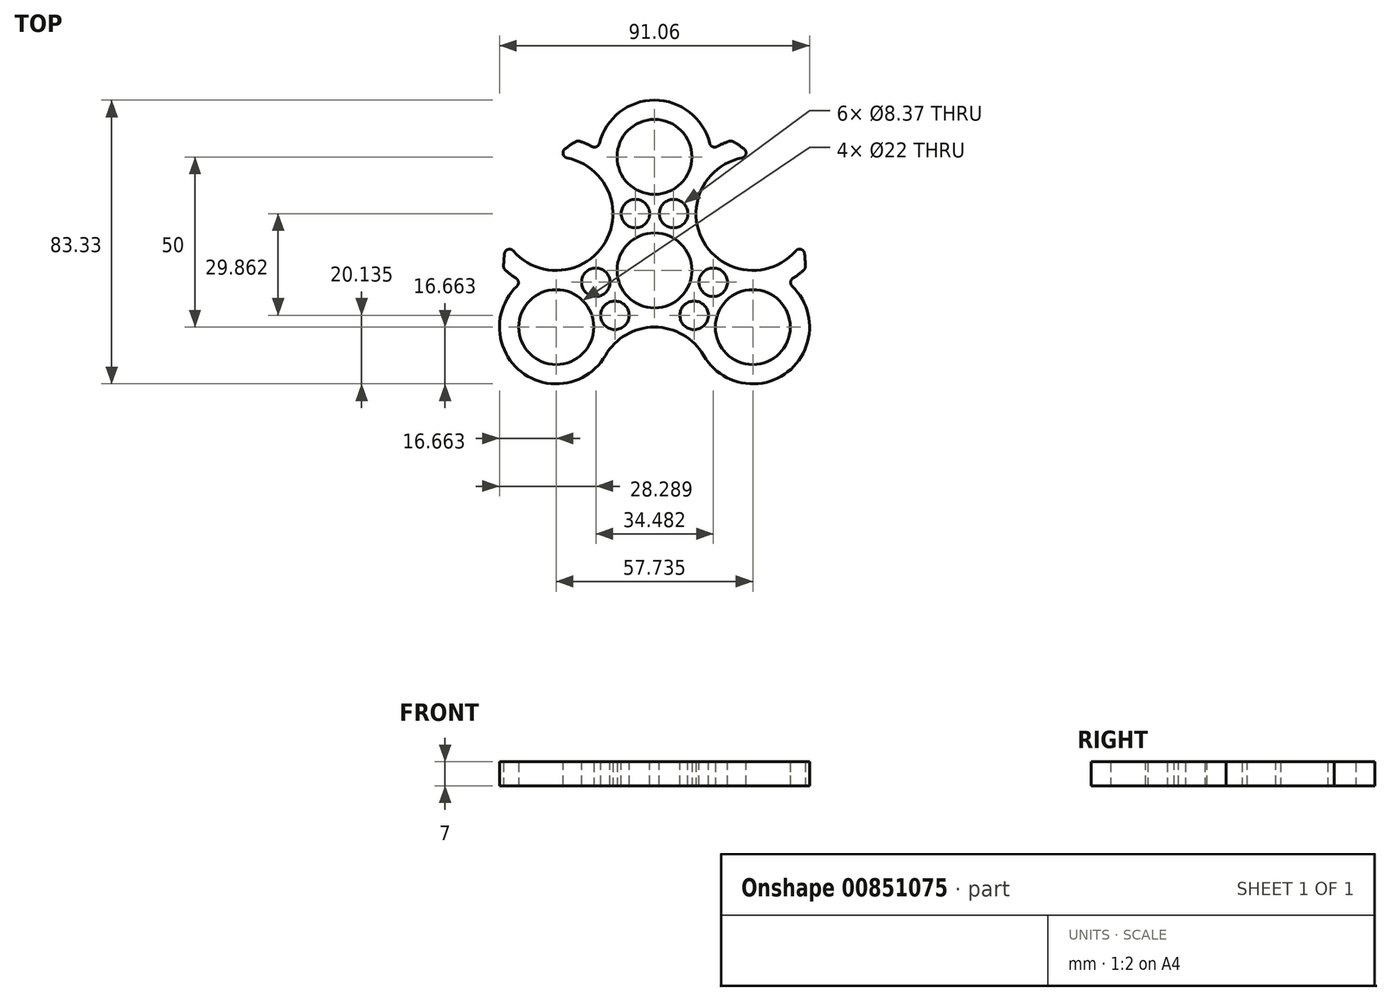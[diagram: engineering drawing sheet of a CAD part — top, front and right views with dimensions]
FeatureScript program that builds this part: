
annotation { "Feature Type Name" : "Feature", "Feature Type Description" : "" }
export const myFeature = defineFeature(function(context is Context, id is Id, definition is map)
    precondition{}
    {
        {
            var Q0;
            Q0=qCreatedBy(makeId("Top.planeOp"),FACE);
            var sketch = newSketch(context, id + "F0", { "sketchPlane" : qUnion([Q0])});
            skCircle(sketch, "E0", {"center": v(0, 0) * mm, "radius": 50 * mm});
            skCircle(sketch, "E1", {"center": v(0, 33.33) * mm, "radius": 16.67 * mm});
            skCircle(sketch, "E2", {"center": v(0, 0) * mm, "radius": 16.67 * mm});
            skLineSegment(sketch, "E3.0", {"start": v(28.87, -16.67) * mm, "end": v(-28.87, -16.67) * mm, "construction": true});
            skLineSegment(sketch, "E3.1", {"start": v(-28.87, -16.67) * mm, "end": v(0, 33.33) * mm, "construction": true});
            skLineSegment(sketch, "E3.2", {"start": v(0, 33.33) * mm, "end": v(28.87, -16.67) * mm, "construction": true});
            skPoint(sketch, "E3.0.midPoint", {"position": v(0, -16.67) * mm});
            skCircle(sketch, "E4", {"center": v(-28.87, -16.67) * mm, "radius": 16.67 * mm});
            skCircle(sketch, "E5", {"center": v(28.87, -16.67) * mm, "radius": 16.67 * mm});
            skArc(sketch, "E6", {"start": v(14.43, -25) * mm, "mid": v(0, -16.67) * mm, "end": v(-14.43, -25) * mm});
            skArc(sketch, "E7", {"start": v(-28.87, 0) * mm, "mid": v(-14.43, 8.33) * mm, "end": v(-14.43, 25) * mm});
            skArc(sketch, "E8", {"start": v(14.43, 25) * mm, "mid": v(14.43, 8.33) * mm, "end": v(28.87, 0) * mm});
            skCircle(sketch, "E9", {"center": v(-28.87, -16.67) * mm, "radius": 11 * mm});
            skCircle(sketch, "E10", {"center": v(0, 0) * mm, "radius": 11 * mm});
            skCircle(sketch, "E11", {"center": v(28.87, -16.67) * mm, "radius": 11 * mm});
            skCircle(sketch, "E12", {"center": v(0, 33.33) * mm, "radius": 11 * mm});
            skSolve(sketch);
        }
        {
            var Q0;
            Q0=makeQuery(id+"F0.imprint","IMPRINT",FACE,{"disambiguationData":[TD([[makeQuery(id+"F0.imprint","IMPRINT",EDGE,{"derivedFrom":sQuery(id+"F0.wireOp",EDGE,"E9")}),-1.0]])]});
            var Q1;
            {var subQ0=sQuery(id+"F0.wireOp",EDGE,"E7");var subQ1=sQuery(id+"F0.wireOp",EDGE,"E2");var subQ2=makeQuery(id+"F0.imprint","INTERSECT",VERTEX,{"derivedFrom":[subQ1,subQ0]});Q1=makeQuery(id+"F0.imprint","IMPRINT",FACE,{"disambiguationData":[TD([[makeQuery(id+"F0.imprint","IMPRINT",EDGE,{"disambiguationData":[TD([[subQ2,-1.0]])],"derivedFrom":subQ1}),-1.0]])]});}
            var Q2;
            Q2=makeQuery(id+"F0.imprint","IMPRINT",FACE,{"disambiguationData":[TD([[makeQuery(id+"F0.imprint","IMPRINT",EDGE,{"derivedFrom":sQuery(id+"F0.wireOp",EDGE,"E10")}),-1.0]])]});
            var Q3;
            Q3=makeQuery(id+"F0.imprint","IMPRINT",FACE,{"disambiguationData":[TD([[makeQuery(id+"F0.imprint","IMPRINT",EDGE,{"derivedFrom":sQuery(id+"F0.wireOp",EDGE,"E11")}),-1.0]])]});
            var Q4;
            Q4=makeQuery(id+"F0.imprint","IMPRINT",FACE,{"disambiguationData":[TD([[makeQuery(id+"F0.imprint","IMPRINT",EDGE,{"derivedFrom":sQuery(id+"F0.wireOp",EDGE,"E12")}),-1.0]])]});
            var Q5;
            {var subQ0=sQuery(id+"F0.wireOp",EDGE,"E7");var subQ1=sQuery(id+"F0.wireOp",EDGE,"E1");var subQ2=makeQuery(id+"F0.imprint","INTERSECT",VERTEX,{"derivedFrom":[subQ1,subQ0]});Q5=makeQuery(id+"F0.imprint","IMPRINT",FACE,{"disambiguationData":[TD([[makeQuery(id+"F0.imprint","IMPRINT",EDGE,{"disambiguationData":[TD([[subQ2,-1.0]])],"derivedFrom":subQ1}),-1.0]])]});}
            var Q6;
            {var subQ0=sQuery(id+"F0.wireOp",EDGE,"E8");var subQ1=sQuery(id+"F0.wireOp",EDGE,"E1");var subQ2=makeQuery(id+"F0.imprint","INTERSECT",VERTEX,{"derivedFrom":[subQ1,subQ0]});Q6=makeQuery(id+"F0.imprint","IMPRINT",FACE,{"disambiguationData":[TD([[makeQuery(id+"F0.imprint","IMPRINT",EDGE,{"disambiguationData":[TD([[subQ2,1.0]])],"derivedFrom":subQ1}),-1.0]])]});}
            var Q7;
            {var subQ0=sQuery(id+"F0.wireOp",EDGE,"E8");var subQ1=sQuery(id+"F0.wireOp",EDGE,"E2");var subQ2=makeQuery(id+"F0.imprint","INTERSECT",VERTEX,{"derivedFrom":[subQ1,subQ0]});Q7=makeQuery(id+"F0.imprint","IMPRINT",FACE,{"disambiguationData":[TD([[makeQuery(id+"F0.imprint","IMPRINT",EDGE,{"disambiguationData":[TD([[subQ2,1.0]])],"derivedFrom":subQ1}),-1.0]])]});}
            var Q8;
            {var subQ0=sQuery(id+"F0.wireOp",EDGE,"E6");var subQ1=sQuery(id+"F0.wireOp",EDGE,"E2");var subQ2=makeQuery(id+"F0.imprint","INTERSECT",VERTEX,{"derivedFrom":[subQ1,subQ0]});Q8=makeQuery(id+"F0.imprint","IMPRINT",FACE,{"disambiguationData":[TD([[makeQuery(id+"F0.imprint","IMPRINT",EDGE,{"disambiguationData":[TD([[subQ2,-1.0]])],"derivedFrom":subQ1}),-1.0]])]});}
            var Q9;
            {var subQ0=sQuery(id+"F0.wireOp",EDGE,"E4");var subQ1=sQuery(id+"F0.wireOp",EDGE,"E2");var subQ2=makeQuery(id+"F0.imprint","INTERSECT",VERTEX,{"derivedFrom":[subQ1,subQ0]});Q9=makeQuery(id+"F0.imprint","IMPRINT",FACE,{"disambiguationData":[TD([[makeQuery(id+"F0.imprint","IMPRINT",EDGE,{"disambiguationData":[TD([[subQ2,-1.0]])],"derivedFrom":subQ1}),-1.0]])]});}
            extrude(context, id + "F1", {"entities" : qUnion([Q0, Q1, Q2, Q3, Q4, Q5, Q6, Q7, Q8, Q9]), "endBound" : BoundingType.SYMMETRIC, "depth" : 7 * mm, "offsetDistance" : 25 * mm});
        }
        {
            var Q0;
            Q0=qCreatedBy(makeId("Top.planeOp"),FACE);
            var sketch = newSketch(context, id + "F2", { "sketchPlane" : qUnion([Q0])});
            skArc(sketch, "E13.0", {"start": v(14.43, -25) * mm, "mid": v(0, -16.67) * mm, "end": v(-14.43, -25) * mm});
            skCircle(sketch, "E14", {"center": v(0, -33.33) * mm, "radius": 16.67 * mm});
            skCircle(sketch, "E15", {"center": v(0, -33.33) * mm, "radius": 22.33 * mm});
            skCircle(sketch, "E16", {"center": v(0, 0) * mm, "radius": 44.33 * mm});
            skCircle(sketch, "E17.1.0", {"center": v(28.87, 16.67) * mm, "radius": 22.33 * mm});
            skCircle(sketch, "E17.1.1", {"center": v(28.87, 16.67) * mm, "radius": 16.67 * mm});
            skCircle(sketch, "E17.2.0", {"center": v(-28.87, 16.67) * mm, "radius": 22.33 * mm});
            skCircle(sketch, "E17.2.1", {"center": v(-28.87, 16.67) * mm, "radius": 16.67 * mm});
            skSolve(sketch);
        }
        {
            var Q0;
            {var subQ0=sQuery(id+"F2.wireOp",EDGE,"E14");var subQ4=makeQuery(id+"F2.imprint","IMPRINT",VERTEX,{"disambiguationData":[OD(0.0)],"derivedFrom":subQ0});Q0=makeQuery(id+"F2.imprint","IMPRINT",FACE,{"disambiguationData":[TD([[makeQuery(id+"F2.imprint","IMPRINT",EDGE,{"disambiguationData":[TD([[subQ4,1.0]])],"derivedFrom":subQ0}),-1.0]])]});}
            var Q1;
            {var subQ0=sQuery(id+"F2.wireOp",EDGE,"E17.2.0");var subQ1=sQuery(id+"F2.wireOp",EDGE,"E16");var subQ2=makeQuery(id+"F2.imprint","INTERSECT",VERTEX,{"disambiguationData":[OD(0.0)],"derivedFrom":[subQ1,subQ0]});Q1=makeQuery(id+"F2.imprint","IMPRINT",FACE,{"disambiguationData":[TD([[makeQuery(id+"F2.imprint","IMPRINT",EDGE,{"disambiguationData":[TD([[subQ2,-1.0]])],"derivedFrom":subQ1}),1.0]])]});}
            var Q2;
            {var subQ0=sQuery(id+"F2.wireOp",EDGE,"E17.1.0");var subQ1=sQuery(id+"F2.wireOp",EDGE,"E16");var subQ2=makeQuery(id+"F2.imprint","INTERSECT",VERTEX,{"disambiguationData":[OD(0.0)],"derivedFrom":[subQ1,subQ0]});Q2=makeQuery(id+"F2.imprint","IMPRINT",FACE,{"disambiguationData":[TD([[makeQuery(id+"F2.imprint","IMPRINT",EDGE,{"disambiguationData":[TD([[subQ2,-1.0]])],"derivedFrom":subQ1}),1.0]])]});}
            extrude(context, id + "F3", {"entities" : qUnion([Q0, Q1, Q2]), "operationType" : NewBodyOperationType.ADD, "endBound" : BoundingType.SYMMETRIC, "depth" : 7 * mm, "offsetDistance" : 25 * mm});
        }
        {
            var Q0;
            {var subQ0=sQuery(id+"F2.wireOp",EDGE,"E17.2.0");var subQ1=sQuery(id+"F2.wireOp",EDGE,"E16");Q0=makeQuery(id+"F3.opExtrude","SWEPT_EDGE",EDGE,{"disambiguationData":[OSD([subQ1,subQ0]),TDD([makeQuery(id+"F2.imprint","INTERSECT",VERTEX,{"disambiguationData":[OD(1.0)],"derivedFrom":[subQ1,subQ0]})])]});}
            var Q1;
            {var subQ0=sQuery(id+"F2.wireOp",EDGE,"E17.2.0");var subQ1=sQuery(id+"F2.wireOp",EDGE,"E16");Q1=makeQuery(id+"F3.opExtrude","SWEPT_EDGE",EDGE,{"disambiguationData":[OSD([subQ1,subQ0]),TDD([makeQuery(id+"F2.imprint","INTERSECT",VERTEX,{"disambiguationData":[OD(0.0)],"derivedFrom":[subQ1,subQ0]})])]});}
            var Q2;
            Q2=makeQuery(id+"F3.boolean.opBoolean","INTERSECT",EDGE,{"derivedFrom":[makeQuery(id+"F1.opExtrude","SWEPT_FACE",FACE,{"disambiguationData":[OSD([sQuery(id+"F0.wireOp",EDGE,"E1")])]}),makeQuery(id+"F3.opExtrude","SWEPT_FACE",FACE,{"disambiguationData":[OSD([sQuery(id+"F2.wireOp",EDGE,"E17.2.0")])]})]});
            var Q3;
            {var subQ0=sQuery(id+"F2.wireOp",EDGE,"E17.2.1");var subQ1=sQuery(id+"F2.wireOp",EDGE,"E16");Q3=makeQuery(id+"F3.opExtrude","SWEPT_EDGE",EDGE,{"disambiguationData":[OSD([subQ1,subQ0]),TDD([makeQuery(id+"F2.imprint","INTERSECT",VERTEX,{"disambiguationData":[OD(0.0)],"derivedFrom":[subQ1,subQ0]})])]});}
            var Q4;
            {var subQ0=sQuery(id+"F2.wireOp",EDGE,"E17.2.1");var subQ1=sQuery(id+"F2.wireOp",EDGE,"E16");Q4=makeQuery(id+"F3.opExtrude","SWEPT_EDGE",EDGE,{"disambiguationData":[OSD([subQ1,subQ0]),TDD([makeQuery(id+"F2.imprint","INTERSECT",VERTEX,{"disambiguationData":[OD(1.0)],"derivedFrom":[subQ1,subQ0]})])]});}
            var Q5;
            Q5=makeQuery(id+"F3.boolean.opBoolean","INTERSECT",EDGE,{"derivedFrom":[makeQuery(id+"F1.opExtrude","SWEPT_FACE",FACE,{"disambiguationData":[OSD([sQuery(id+"F0.wireOp",EDGE,"E4")])]}),makeQuery(id+"F3.opExtrude","SWEPT_FACE",FACE,{"disambiguationData":[OSD([sQuery(id+"F2.wireOp",EDGE,"E17.2.0")])]})]});
            var Q6;
            Q6=makeQuery(id+"F3.boolean.opBoolean","INTERSECT",EDGE,{"derivedFrom":[makeQuery(id+"F1.opExtrude","SWEPT_FACE",FACE,{"disambiguationData":[OSD([sQuery(id+"F0.wireOp",EDGE,"E4")])]}),makeQuery(id+"F3.opExtrude","SWEPT_FACE",FACE,{"disambiguationData":[OSD([sQuery(id+"F2.wireOp",EDGE,"E15")])]})]});
            var Q7;
            {var subQ0=sQuery(id+"F2.wireOp",EDGE,"E16");var subQ1=sQuery(id+"F2.wireOp",EDGE,"E15");Q7=makeQuery(id+"F3.opExtrude","SWEPT_EDGE",EDGE,{"disambiguationData":[OSD([subQ1,subQ0]),TDD([makeQuery(id+"F2.imprint","INTERSECT",VERTEX,{"disambiguationData":[OD(0.0)],"derivedFrom":[subQ1,subQ0]})])]});}
            var Q8;
            {var subQ0=sQuery(id+"F2.wireOp",EDGE,"E16");var subQ1=sQuery(id+"F2.wireOp",EDGE,"E14");Q8=makeQuery(id+"F3.opExtrude","SWEPT_EDGE",EDGE,{"disambiguationData":[OSD([subQ1,subQ0]),TDD([makeQuery(id+"F2.imprint","INTERSECT",VERTEX,{"disambiguationData":[OD(0.0)],"derivedFrom":[subQ1,subQ0]})])]});}
            var Q9;
            {var subQ0=sQuery(id+"F2.wireOp",EDGE,"E16");var subQ1=sQuery(id+"F2.wireOp",EDGE,"E14");Q9=makeQuery(id+"F3.opExtrude","SWEPT_EDGE",EDGE,{"disambiguationData":[OSD([subQ1,subQ0]),TDD([makeQuery(id+"F2.imprint","INTERSECT",VERTEX,{"disambiguationData":[OD(1.0)],"derivedFrom":[subQ1,subQ0]})])]});}
            var Q10;
            {var subQ0=sQuery(id+"F2.wireOp",EDGE,"E16");var subQ1=sQuery(id+"F2.wireOp",EDGE,"E15");Q10=makeQuery(id+"F3.opExtrude","SWEPT_EDGE",EDGE,{"disambiguationData":[OSD([subQ1,subQ0]),TDD([makeQuery(id+"F2.imprint","INTERSECT",VERTEX,{"disambiguationData":[OD(1.0)],"derivedFrom":[subQ1,subQ0]})])]});}
            var Q11;
            Q11=makeQuery(id+"F3.boolean.opBoolean","INTERSECT",EDGE,{"derivedFrom":[makeQuery(id+"F1.opExtrude","SWEPT_FACE",FACE,{"disambiguationData":[OSD([sQuery(id+"F0.wireOp",EDGE,"E5")])]}),makeQuery(id+"F3.opExtrude","SWEPT_FACE",FACE,{"disambiguationData":[OSD([sQuery(id+"F2.wireOp",EDGE,"E15")])]})]});
            var Q12;
            Q12=makeQuery(id+"F3.boolean.opBoolean","INTERSECT",EDGE,{"derivedFrom":[makeQuery(id+"F1.opExtrude","SWEPT_FACE",FACE,{"disambiguationData":[OSD([sQuery(id+"F0.wireOp",EDGE,"E5")])]}),makeQuery(id+"F3.opExtrude","SWEPT_FACE",FACE,{"disambiguationData":[OSD([sQuery(id+"F2.wireOp",EDGE,"E17.1.0")])]})]});
            var Q13;
            {var subQ0=sQuery(id+"F2.wireOp",EDGE,"E17.1.0");var subQ1=sQuery(id+"F2.wireOp",EDGE,"E16");Q13=makeQuery(id+"F3.opExtrude","SWEPT_EDGE",EDGE,{"disambiguationData":[OSD([subQ1,subQ0]),TDD([makeQuery(id+"F2.imprint","INTERSECT",VERTEX,{"disambiguationData":[OD(0.0)],"derivedFrom":[subQ1,subQ0]})])]});}
            var Q14;
            {var subQ0=sQuery(id+"F2.wireOp",EDGE,"E17.1.1");var subQ1=sQuery(id+"F2.wireOp",EDGE,"E16");Q14=makeQuery(id+"F3.opExtrude","SWEPT_EDGE",EDGE,{"disambiguationData":[OSD([subQ1,subQ0]),TDD([makeQuery(id+"F2.imprint","INTERSECT",VERTEX,{"disambiguationData":[OD(0.0)],"derivedFrom":[subQ1,subQ0]})])]});}
            var Q15;
            {var subQ0=sQuery(id+"F2.wireOp",EDGE,"E17.1.1");var subQ1=sQuery(id+"F2.wireOp",EDGE,"E16");Q15=makeQuery(id+"F3.opExtrude","SWEPT_EDGE",EDGE,{"disambiguationData":[OSD([subQ1,subQ0]),TDD([makeQuery(id+"F2.imprint","INTERSECT",VERTEX,{"disambiguationData":[OD(1.0)],"derivedFrom":[subQ1,subQ0]})])]});}
            var Q16;
            {var subQ0=sQuery(id+"F2.wireOp",EDGE,"E17.1.0");var subQ1=sQuery(id+"F2.wireOp",EDGE,"E16");Q16=makeQuery(id+"F3.opExtrude","SWEPT_EDGE",EDGE,{"disambiguationData":[OSD([subQ1,subQ0]),TDD([makeQuery(id+"F2.imprint","INTERSECT",VERTEX,{"disambiguationData":[OD(1.0)],"derivedFrom":[subQ1,subQ0]})])]});}
            var Q17;
            Q17=makeQuery(id+"F3.boolean.opBoolean","INTERSECT",EDGE,{"derivedFrom":[makeQuery(id+"F1.opExtrude","SWEPT_FACE",FACE,{"disambiguationData":[OSD([sQuery(id+"F0.wireOp",EDGE,"E1")])]}),makeQuery(id+"F3.opExtrude","SWEPT_FACE",FACE,{"disambiguationData":[OSD([sQuery(id+"F2.wireOp",EDGE,"E17.1.0")])]})]});
            fillet(context, id + "F4", {"entities" : qUnion([Q0, Q1, Q2, Q3, Q4, Q5, Q6, Q7, Q8, Q9, Q10, Q11, Q12, Q13, Q14, Q15, Q16, Q17]), "radius" : 1.5 * mm, "tangentPropagation" : true, "allowEdgeOverflow" : false});
        }
        {
            var Q0;
            {var subQ0=sQuery(id+"F2.wireOp",EDGE,"E16");Q0=makeQuery(id+"F3.boolean.opBoolean","MERGE",FACE,{"derivedFrom":[makeQuery(id+"F1.opExtrude","CAP_FACE",FACE,{"disambiguationData":[OSD([sQuery(id+"F0.wireOp",EDGE,"E1"),sQuery(id+"F0.wireOp",EDGE,"E4"),sQuery(id+"F0.wireOp",EDGE,"E5"),sQuery(id+"F0.wireOp",EDGE,"E6"),sQuery(id+"F0.wireOp",EDGE,"E7"),sQuery(id+"F0.wireOp",EDGE,"E8"),sQuery(id+"F0.wireOp",EDGE,"E9"),sQuery(id+"F0.wireOp",EDGE,"E10"),sQuery(id+"F0.wireOp",EDGE,"E11"),sQuery(id+"F0.wireOp",EDGE,"E12")])],"isStart":false}),makeQuery(id+"F3.opExtrude","CAP_FACE",FACE,{"disambiguationData":[OSD([sQuery(id+"F2.wireOp",EDGE,"E14"),sQuery(id+"F2.wireOp",EDGE,"E15"),subQ0])],"isStart":false}),makeQuery(id+"F3.opExtrude","CAP_FACE",FACE,{"disambiguationData":[OSD([subQ0,sQuery(id+"F2.wireOp",EDGE,"E17.1.0"),sQuery(id+"F2.wireOp",EDGE,"E17.1.1")])],"isStart":false}),makeQuery(id+"F3.opExtrude","CAP_FACE",FACE,{"disambiguationData":[OSD([subQ0,sQuery(id+"F2.wireOp",EDGE,"E17.2.0"),sQuery(id+"F2.wireOp",EDGE,"E17.2.1")])],"isStart":false})]});}
            var sketch = newSketch(context, id + "F5", { "sketchPlane" : qUnion([Q0])});
            skArc(sketch, "E18.0", {"start": v(-43.25, 4.15) * mm, "mid": v(-12.36, 7.13) * mm, "end": v(-25.22, 35.38) * mm, "construction": true});
            skCircle(sketch, "E19.0", {"center": v(-28.87, -16.67) * mm, "radius": 13.4 * mm, "construction": true});
            skCircle(sketch, "E20.0", {"center": v(0, 0) * mm, "radius": 13.4 * mm, "construction": true});
            skArc(sketch, "E21.0", {"start": v(18.03, -39.53) * mm, "mid": v(0, -14.27) * mm, "end": v(-18.03, -39.53) * mm, "construction": true});
            skCircle(sketch, "E22", {"center": v(-11.63, -13.2) * mm, "radius": 4.19 * mm});
            skCircle(sketch, "E23", {"center": v(-17.24, -3.47) * mm, "radius": 4.19 * mm});
            skCircle(sketch, "E24.1.0", {"center": v(11.63, -13.2) * mm, "radius": 4.19 * mm});
            skCircle(sketch, "E24.1.1", {"center": v(17.24, -3.47) * mm, "radius": 4.19 * mm});
            skCircle(sketch, "E24.2.0", {"center": v(5.61, 16.67) * mm, "radius": 4.19 * mm});
            skCircle(sketch, "E24.2.1", {"center": v(-5.61, 16.67) * mm, "radius": 4.19 * mm});
            skSolve(sketch);
        }
        {
            var Q0;
            Q0=makeQuery(id+"F5.imprint","IMPRINT",FACE,{"disambiguationData":[TD([[makeQuery(id+"F5.imprint","IMPRINT",EDGE,{"derivedFrom":sQuery(id+"F5.wireOp",EDGE,"E23")}),1.0]])]});
            var Q1;
            Q1=makeQuery(id+"F5.imprint","IMPRINT",FACE,{"disambiguationData":[TD([[makeQuery(id+"F5.imprint","IMPRINT",EDGE,{"derivedFrom":sQuery(id+"F5.wireOp",EDGE,"E24.2.1")}),1.0]])]});
            var Q2;
            Q2=makeQuery(id+"F5.imprint","IMPRINT",FACE,{"disambiguationData":[TD([[makeQuery(id+"F5.imprint","IMPRINT",EDGE,{"derivedFrom":sQuery(id+"F5.wireOp",EDGE,"E24.2.0")}),1.0]])]});
            var Q3;
            Q3=makeQuery(id+"F5.imprint","IMPRINT",FACE,{"disambiguationData":[TD([[makeQuery(id+"F5.imprint","IMPRINT",EDGE,{"derivedFrom":sQuery(id+"F5.wireOp",EDGE,"E24.1.1")}),1.0]])]});
            var Q4;
            Q4=makeQuery(id+"F5.imprint","IMPRINT",FACE,{"disambiguationData":[TD([[makeQuery(id+"F5.imprint","IMPRINT",EDGE,{"derivedFrom":sQuery(id+"F5.wireOp",EDGE,"E24.1.0")}),1.0]])]});
            var Q5;
            Q5=makeQuery(id+"F5.imprint","IMPRINT",FACE,{"disambiguationData":[TD([[makeQuery(id+"F5.imprint","IMPRINT",EDGE,{"derivedFrom":sQuery(id+"F5.wireOp",EDGE,"E22")}),1.0]])]});
            extrude(context, id + "F6", {"entities" : qUnion([Q0, Q1, Q2, Q3, Q4, Q5]), "operationType" : NewBodyOperationType.REMOVE, "oppositeDirection" : true, "depth" : 25 * mm, "offsetDistance" : 25 * mm});
        }
    });
